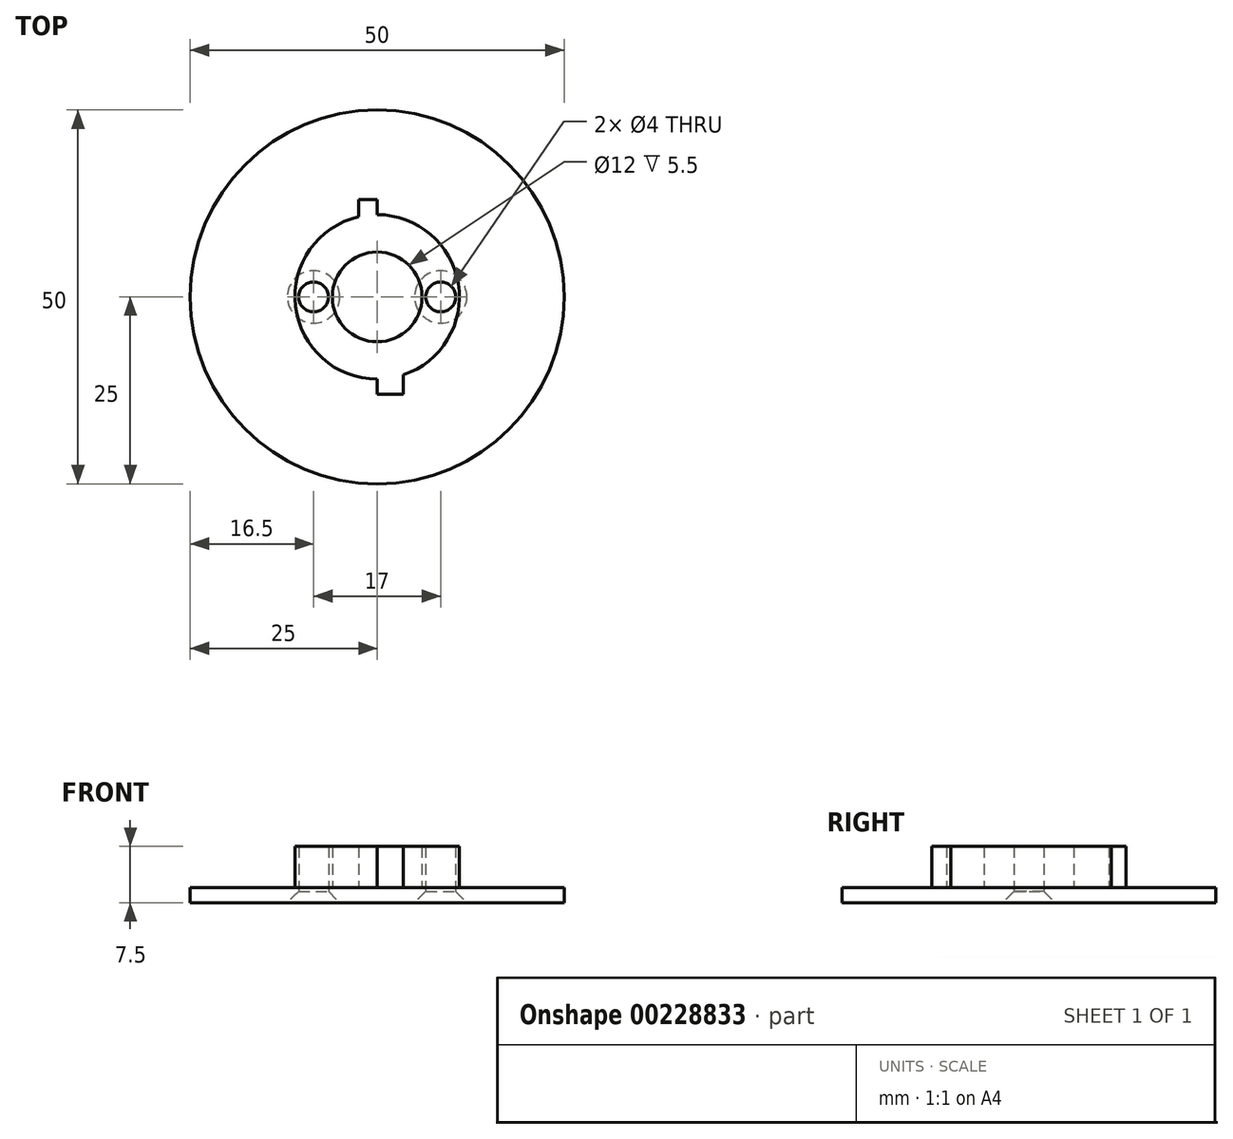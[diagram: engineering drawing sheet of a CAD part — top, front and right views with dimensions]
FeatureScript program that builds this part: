
annotation { "Feature Type Name" : "Feature", "Feature Type Description" : "" }
export const myFeature = defineFeature(function(context is Context, id is Id, definition is map)
    precondition{}
    {
        {
            var Q0;
            Q0=qCreatedBy(makeId("Top.planeOp"),FACE);
            var sketch = newSketch(context, id + "F0", { "sketchPlane" : qUnion([Q0])});
            skCircle(sketch, "E0", {"center": v(0, 0) * mm, "radius": 25 * mm});
            skCircle(sketch, "E1", {"center": v(0, 0) * mm, "radius": 11 * mm});
            skCircle(sketch, "E2", {"center": v(0, 0) * mm, "radius": 6 * mm});
            skLineSegment(sketch, "E3", {"start": v(0, 11) * mm, "end": v(0, 13) * mm});
            skLineSegment(sketch, "E4", {"start": v(0, 13) * mm, "end": v(-2.5, 13) * mm});
            skLineSegment(sketch, "E5", {"start": v(-2.5, 13) * mm, "end": v(-2.5, 10.71) * mm});
            skLineSegment(sketch, "E6", {"start": v(0, -11) * mm, "end": v(0, -13) * mm});
            skLineSegment(sketch, "E7", {"start": v(0, -13) * mm, "end": v(3.5, -13) * mm});
            skLineSegment(sketch, "E8", {"start": v(3.5, -13) * mm, "end": v(3.5, -10.43) * mm});
            skSolve(sketch);
        }
        {
            var Q0;
            Q0=makeQuery(id+"F0.imprint","IMPRINT",FACE,{"disambiguationData":[TD([[makeQuery(id+"F0.imprint","IMPRINT",EDGE,{"derivedFrom":sQuery(id+"F0.wireOp",EDGE,"E0")}),1.0]])]});
            var Q1;
            Q1=makeQuery(id+"F0.imprint","IMPRINT",FACE,{"disambiguationData":[TD([[makeQuery(id+"F0.imprint","IMPRINT",EDGE,{"derivedFrom":sQuery(id+"F0.wireOp",EDGE,"E1")}),1.0]])]});
            var Q2;
            Q2=makeQuery(id+"F0.imprint","IMPRINT",FACE,{"disambiguationData":[TD([[makeQuery(id+"F0.imprint","IMPRINT",EDGE,{"derivedFrom":sQuery(id+"F0.wireOp",EDGE,"E2")}),1.0]])]});
            var Q3;
            {var subQ0=sQuery(id+"F0.wireOp",EDGE,"E3");Q3=makeQuery(id+"F0.imprint","IMPRINT",FACE,{"disambiguationData":[TD([[makeQuery(id+"F0.imprint","IMPRINT",EDGE,{"derivedFrom":subQ0}),1.0]])]});}
            var Q4;
            {var subQ0=sQuery(id+"F0.wireOp",EDGE,"E6");Q4=makeQuery(id+"F0.imprint","IMPRINT",FACE,{"disambiguationData":[TD([[makeQuery(id+"F0.imprint","IMPRINT",EDGE,{"derivedFrom":subQ0}),1.0]])]});}
            extrude(context, id + "F1", {"entities" : qUnion([Q0, Q1, Q2, Q3, Q4]), "depth" : 2 * mm});
        }
        {
            var Q0;
            Q0=makeQuery(id+"F0.imprint","IMPRINT",FACE,{"disambiguationData":[TD([[makeQuery(id+"F0.imprint","IMPRINT",EDGE,{"derivedFrom":sQuery(id+"F0.wireOp",EDGE,"E1")}),1.0]])]});
            var Q1;
            {var subQ0=sQuery(id+"F0.wireOp",EDGE,"E6");Q1=makeQuery(id+"F0.imprint","IMPRINT",FACE,{"disambiguationData":[TD([[makeQuery(id+"F0.imprint","IMPRINT",EDGE,{"derivedFrom":subQ0}),1.0]])]});}
            var Q2;
            {var subQ0=sQuery(id+"F0.wireOp",EDGE,"E3");Q2=makeQuery(id+"F0.imprint","IMPRINT",FACE,{"disambiguationData":[TD([[makeQuery(id+"F0.imprint","IMPRINT",EDGE,{"derivedFrom":subQ0}),1.0]])]});}
            extrude(context, id + "F2", {"entities" : qUnion([Q0, Q1, Q2]), "operationType" : NewBodyOperationType.ADD, "depth" : 7.5 * mm});
        }
        {
            var Q0;
            Q0=makeQuery(id+"F2.opExtrude","CAP_FACE",FACE,{"disambiguationData":[OSD([sQuery(id+"F0.wireOp",EDGE,"E1"),sQuery(id+"F0.wireOp",EDGE,"E2")])],"isStart":false});
            var sketch = newSketch(context, id + "F3", { "sketchPlane" : qUnion([Q0])});
            skSolve(sketch);
        }
        {
            var Q0;
            Q0=makeQuery(id+"F0.imprint","IMPRINT",FACE,{"disambiguationData":[TD([[makeQuery(id+"F0.imprint","IMPRINT",EDGE,{"derivedFrom":sQuery(id+"F0.wireOp",EDGE,"E0")}),1.0]])]});
            var sketch = newSketch(context, id + "F4", { "sketchPlane" : qUnion([Q0])});
            skPoint(sketch, "E9", {"position": v(8.5, 0) * mm});
            skPoint(sketch, "E10", {"position": v(-8.5, 0) * mm});
            skSolve(sketch);
        }
        {
            var Q0;
            Q0=sQuery(id+"F3.wireOp",VERTEX,"a7a045d3-eeee-4543-874e-eeae766dbf93");
            var Q1;
            Q1=sQuery(id+"F3.wireOp",VERTEX,"2bbd740c-ef9f-4c35-a09d-2c441b071d0a");
            var Q2;
            Q2=sQuery(id+"F4.wireOp",VERTEX,"E10");
            var Q3;
            Q3=sQuery(id+"F4.wireOp",VERTEX,"E9");
            var Q4;
            Q4=makeQuery(id+"F1.opExtrude","SWEPT_BODY",BODY,{"disambiguationData":[OSD([sQuery(id+"F0.wireOp",EDGE,"E0")])]});
            hole(context, id + "F5", {"style" : HoleStyle.C_SINK, "endStyle" : HoleEndStyle.THROUGH, "oppositeDirection" : true, "holeDiameter" : 4 * mm, "cSinkDiameter" : 7 * mm, "cSinkAngle" : 90 * degree, "startFromSketch" : true, "locations" : qUnion([Q0, Q1, Q2, Q3]), "scope" : qUnion([Q4]), "isTappedThrough" : true});
        }
    });
